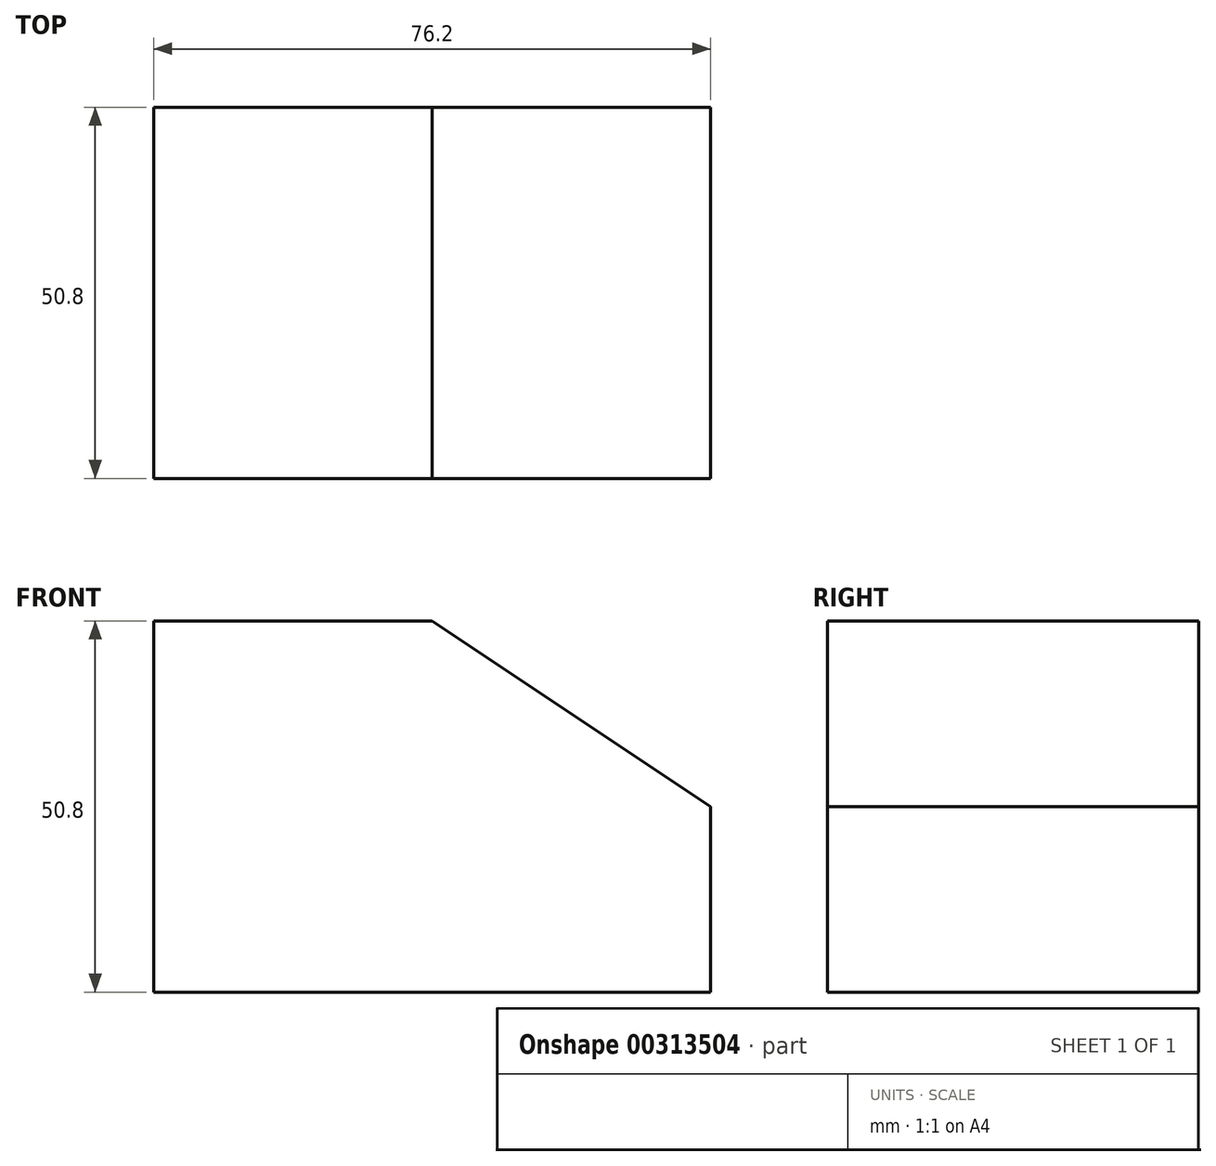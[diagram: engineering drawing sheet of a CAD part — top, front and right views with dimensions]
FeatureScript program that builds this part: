
annotation { "Feature Type Name" : "Feature", "Feature Type Description" : "" }
export const myFeature = defineFeature(function(context is Context, id is Id, definition is map)
    precondition{}
    {
        {
            var Q0;
            Q0=qCreatedBy(makeId("Front.planeOp"),FACE);
            var sketch = newSketch(context, id + "F0", { "sketchPlane" : qUnion([Q0])});
            skLineSegment(sketch, "E0", {"start": v(-49.4, 31.93) * mm, "end": v(-49.4, -18.87) * mm});
            skLineSegment(sketch, "E1", {"start": v(-49.4, -18.87) * mm, "end": v(26.8, -18.87) * mm});
            skLineSegment(sketch, "E2", {"start": v(26.8, -18.87) * mm, "end": v(26.8, 6.53) * mm});
            skLineSegment(sketch, "E3", {"start": v(-49.4, 31.93) * mm, "end": v(-11.3, 31.93) * mm});
            skLineSegment(sketch, "E4", {"start": v(-11.3, 31.93) * mm, "end": v(26.8, 6.53) * mm});
            skSolve(sketch);
        }
        {
            var Q0;
            Q0 = qSketchRegion(id + "F0", true);
            extrude(context, id + "F1", {"entities" : qUnion([Q0]), "depth" : 50.8 * mm});
        }
    });
